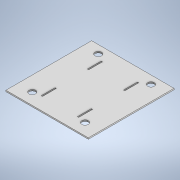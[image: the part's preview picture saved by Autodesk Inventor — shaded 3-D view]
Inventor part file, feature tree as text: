
AUTODESK INVENTOR PART (.ipt)
format: ipt  version: 2022 (Build 260153000, 153)  size: 155,136 bytes
history: native  units: mm
features: extrude x2, sketch x2, projected_geometry x1
ambient origin geometry x8: Origin, YZ Plane, XZ Plane, XY Plane, X Axis, Y Axis, Z Axis, Center Point
bodies: Solid1 (feature_tree)
feature tree (5):
  extrude  "Extrusion1"  Depth=125.0mm
  extrude  "Extrusion2"  Depth=10.0mm
  sketch  "Sketch1"  dims[d0=130.0mm d1=125.0mm]
  sketch  "Sketch2"  dims[d2=10.0mm d3=10.0mm d4=100.0mm d5=10.0mm d6=10.0mm d7=100.0mm d8=80.0mm d9=80.0mm d10=17.5mm d11=22.5mm d12=17.5mm d13=22.5mm d14=2.0mm d15=0.0mm d16=53.0mm d17=100.0mm d18=125.0mm d19=36.0mm d20=2.0mm d21=2.0mm d22=2.0mm d23=2.0mm d24=21.0mm d25=21.0mm d26=21.0mm d27=21.0mm d28=19.5mm d29=19.5mm d30=19.5mm d31=19.5mm d32=0.0mm d33=0.0mm]
  projected_geometry  "Projected Loop1"
